# Revit family: Door-Single-Lead_Lined_RPP
name_source: partatom
category: Doors
units: mm (PartAtom-declared; Revit-internal decimal feet)

## family parameters
Always vertical = Yes
Classification Number = 23.75.70.17.17
Cut with Voids When Loaded = No
Host = Wall
Room Calculation Point = No
Shared = No

## types (4) — shared parameters
Assembly Code = F1030200
Construction Details = http://www.arcat.com
Door Closer = Alluminium
Door Frame = Alluminium
Door Panel = Wood
Fire Rating = As Specified in 13 49 00
Function = Interior
Glass Frame = Metal
Glass Panel = Glass
Green Building-LEED = http://www.arcat.com
Keynote = 13 49 00
Manufacturer = Radiation Protection Products, Inc.
Manufacturer Fax = 866-554-8445
Manufacturer Website = http://www.radiationproducts.com
Panel Height = 3' - 0"
Panel Width = 0' - 6"
Product Data = http://www.arcat.com
Product Properties = http://www.arcat.com
Revision = R1_04-2010
Sales Information = http://www.radiationproducts.com
Send Message = http://www.arcat.com
SpecWizard = http://www.arcat.com
Specification = http://www.arcat.com
Test Data = http://www.radiationproducts.com
URL = http://www.radiationproducts.com
Wall Closure = By host
zero-valued in all types: Expected Lifespan (Years), Maintenance Schedule (Months), Warranty Duration (Years)

## per-type parameters (varying)
| type | Description | Height | Model | Width |
| 34" x 80" | Radiation Protection Products Single Door - 2-10 x 6-8 | 6' - 8" | 2'-10" x 6'-8" | 2' - 10" |
| 36" x 80" | Radiation Protection Products Single Door - 3-0 x 6-8 | 6' - 8" | 3'-0" x 6'-8" | 3' - 0" |
| 34" x 84" | Radiation Protection Products Single Door - 2-10 x 7-0 | 7' - 0" | 2'-10" x 7'-0" | 2' - 10" |
| 36" x 84" | Radiation Protection Products Single Door - 3-0 x 7-0 | 7' - 0" | 3'-0" x 7'-0" | 3' - 0" |

## geometry (parser evidence)
native form markers: Blend x10, Sweep x2
no freeform markers — native parametric forms only
